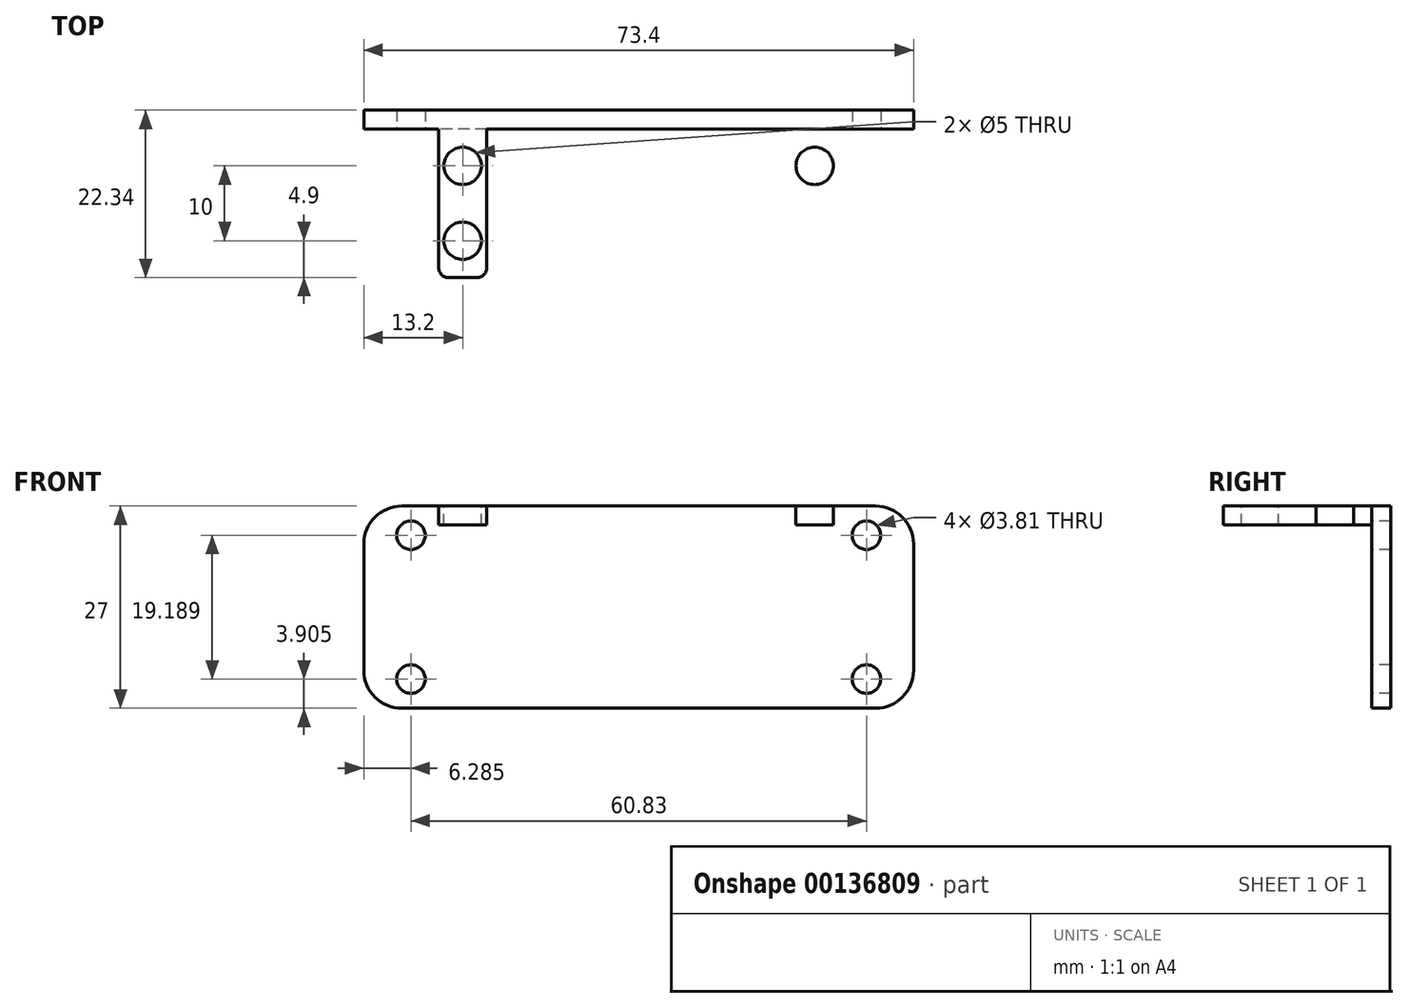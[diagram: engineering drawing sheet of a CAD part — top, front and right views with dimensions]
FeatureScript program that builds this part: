
annotation { "Feature Type Name" : "Feature", "Feature Type Description" : "" }
export const myFeature = defineFeature(function(context is Context, id is Id, definition is map)
    precondition{}
    {
        {
            var Q0;
            Q0=qCreatedBy(makeId("Top.planeOp"),FACE);
            var sketch = newSketch(context, id + "F0", { "sketchPlane" : qUnion([Q0])});
            skLineSegment(sketch, "E0.bottom", {"start": v(26.7, 1.27) * mm, "end": v(-26.7, 1.27) * mm});
            skLineSegment(sketch, "E0.top", {"start": v(26.7, -1.27) * mm, "end": v(-26.7, -1.27) * mm});
            skPoint(sketch, "E0.middle", {"position": v(0, 0) * mm});
            skLineSegment(sketch, "E1", {"start": v(-20.3, -1.27) * mm, "end": v(-20.3, -21.07) * mm});
            skLineSegment(sketch, "E2.bottom", {"start": v(-20.3, -21.07) * mm, "end": v(-26.7, -21.07) * mm});
            skLineSegment(sketch, "E2.top", {"start": v(-20.3, -1.27) * mm, "end": v(-26.7, -1.27) * mm});
            skLineSegment(sketch, "E2.left", {"start": v(-20.3, -21.07) * mm, "end": v(-20.3, -1.27) * mm});
            skLineSegment(sketch, "E2.right", {"start": v(-26.7, -21.07) * mm, "end": v(-26.7, -1.27) * mm});
            skCircle(sketch, "E3", {"center": v(-23.5, -6.17) * mm, "radius": 2.5 * mm});
            skCircle(sketch, "E4", {"center": v(-23.5, -16.17) * mm, "radius": 2.5 * mm});
            skLineSegment(sketch, "E5.bottom", {"start": v(-26.7, 1.27) * mm, "end": v(-36.7, 1.27) * mm});
            skLineSegment(sketch, "E5.top", {"start": v(-26.7, -1.27) * mm, "end": v(-36.7, -1.27) * mm});
            skLineSegment(sketch, "E5.right", {"start": v(-36.7, 1.27) * mm, "end": v(-36.7, -1.27) * mm});
            skLineSegment(sketch, "E6.MirrorCS", {"start": v(26.7, 1.27) * mm, "end": v(36.7, 1.27) * mm});
            skLineSegment(sketch, "E7.MirrorCS", {"start": v(36.7, 1.27) * mm, "end": v(36.7, -1.27) * mm});
            skLineSegment(sketch, "E8.MirrorCS", {"start": v(26.7, -1.27) * mm, "end": v(36.7, -1.27) * mm});
            skCircle(sketch, "E9.MirrorC", {"center": v(23.5, -6.17) * mm, "radius": 2.5 * mm});
            skLineSegment(sketch, "E10.MirrorCS", {"start": v(20.3, -21.07) * mm, "end": v(20.3, -1.27) * mm});
            skLineSegment(sketch, "E11.MirrorCS", {"start": v(26.7, -21.07) * mm, "end": v(26.7, -1.27) * mm});
            skLineSegment(sketch, "E12.MirrorCS", {"start": v(20.3, -21.07) * mm, "end": v(26.7, -21.07) * mm});
            skCircle(sketch, "E13.MirrorC", {"center": v(23.5, -16.17) * mm, "radius": 2.5 * mm});
            skSolve(sketch);
        }
        {
            var Q0;
            Q0=makeQuery(id+"F0.imprint","IMPRINT",FACE,{"disambiguationData":[TD([[makeQuery(id+"F0.imprint","IMPRINT",EDGE,{"derivedFrom":sQuery(id+"F0.wireOp",EDGE,"E0.bottom")}),1.0]])]});
            extrude(context, id + "F1", {"entities" : qUnion([Q0]), "oppositeDirection" : true, "depth" : 27 * mm});
        }
        {
            var Q0;
            Q0=makeQuery(id+"F0.imprint","IMPRINT",FACE,{"disambiguationData":[TD([[makeQuery(id+"F0.imprint","IMPRINT",EDGE,{"derivedFrom":sQuery(id+"F0.wireOp",EDGE,"E2.bottom")}),-1.0]])]});
            var Q1;
            Q1=makeQuery(id+"F0.imprint","IMPRINT",FACE,{"disambiguationData":[TD([[makeQuery(id+"F0.imprint","IMPRINT",EDGE,{"derivedFrom":sQuery(id+"F0.wireOp",EDGE,"E9.MirrorC")}),1.0]])]});
            extrude(context, id + "F2", {"entities" : qUnion([Q0, Q1]), "operationType" : NewBodyOperationType.ADD, "oppositeDirection" : true, "depth" : 2.54 * mm});
        }
        {
            var Q0;
            Q0=makeQuery(id+"F1.opExtrude","CAP_EDGE",EDGE,{"disambiguationData":[OSD([sQuery(id+"F0.wireOp",EDGE,"E5.right")])],"isStart":true});
            var Q1;
            Q1=makeQuery(id+"F1.opExtrude","CAP_EDGE",EDGE,{"disambiguationData":[OSD([sQuery(id+"F0.wireOp",EDGE,"E7.MirrorCS")])],"isStart":true});
            var Q2;
            Q2=makeQuery(id+"F1.opExtrude","CAP_EDGE",EDGE,{"disambiguationData":[OSD([sQuery(id+"F0.wireOp",EDGE,"E7.MirrorCS")])],"isStart":false});
            var Q3;
            Q3=makeQuery(id+"F1.opExtrude","CAP_EDGE",EDGE,{"disambiguationData":[OSD([sQuery(id+"F0.wireOp",EDGE,"E5.right")])],"isStart":false});
            fillet(context, id + "F3", {"entities" : qUnion([Q0, Q1, Q2, Q3]), "radius" : 5.08 * mm, "tangentPropagation" : true, "allowEdgeOverflow" : false});
        }
        {
            var Q0;
            Q0=makeQuery(id+"F1.opExtrude","SWEPT_FACE",FACE,{"disambiguationData":[OSD([sQuery(id+"F0.wireOp",EDGE,"E0.top"),sQuery(id+"F0.wireOp",EDGE,"E2.top"),sQuery(id+"F0.wireOp",EDGE,"E5.top"),sQuery(id+"F0.wireOp",EDGE,"E8.MirrorCS")])]});
            var sketch = newSketch(context, id + "F4", { "sketchPlane" : qUnion([Q0])});
            skLineSegment(sketch, "E14", {"start": v(0, 0) * mm, "end": v(0, -27) * mm});
            skLineSegment(sketch, "E15.bottom", {"start": v(30.42, -3.9) * mm, "end": v(-30.42, -3.9) * mm});
            skLineSegment(sketch, "E15.top", {"start": v(30.42, -23.1) * mm, "end": v(-30.42, -23.1) * mm});
            skLineSegment(sketch, "E15.left", {"start": v(30.42, -3.9) * mm, "end": v(30.42, -23.1) * mm});
            skLineSegment(sketch, "E15.right", {"start": v(-30.42, -3.9) * mm, "end": v(-30.42, -23.1) * mm});
            skPoint(sketch, "E15.middle", {"position": v(0, -13.5) * mm});
            skSolve(sketch);
        }
        {
            var Q0;
            Q0=sQuery(id+"F4.wireOp",VERTEX,"E15.right.start");
            var Q1;
            Q1=sQuery(id+"F4.wireOp",VERTEX,"E15.right.end");
            var Q2;
            Q2=sQuery(id+"F4.wireOp",VERTEX,"E15.left.start");
            var Q3;
            Q3=sQuery(id+"F4.wireOp",VERTEX,"E15.left.end");
            var Q4;
            Q4=makeQuery(id+"F1.opExtrude","SWEPT_BODY",BODY,{"disambiguationData":[OSD([sQuery(id+"F0.wireOp",EDGE,"E0.bottom"),sQuery(id+"F0.wireOp",EDGE,"E0.top"),sQuery(id+"F0.wireOp",EDGE,"E2.top"),sQuery(id+"F0.wireOp",EDGE,"E5.bottom"),sQuery(id+"F0.wireOp",EDGE,"E5.top"),sQuery(id+"F0.wireOp",EDGE,"E5.right"),sQuery(id+"F0.wireOp",EDGE,"E6.MirrorCS"),sQuery(id+"F0.wireOp",EDGE,"E7.MirrorCS"),sQuery(id+"F0.wireOp",EDGE,"E8.MirrorCS")])]});
            hole(context, id + "F5", {"style" : HoleStyle.SIMPLE, "endStyle" : HoleEndStyle.THROUGH, "holeDiameter" : 3.8 * mm, "locations" : qUnion([Q0, Q1, Q2, Q3]), "scope" : qUnion([Q4]), "isTappedThrough" : true});
        }
        {
            var Q0;
            Q0=makeQuery(id+"F2.opExtrude","SWEPT_EDGE",EDGE,{"disambiguationData":[OSD([sQuery(id+"F0.wireOp",EDGE,"E2.bottom"),sQuery(id+"F0.wireOp",EDGE,"E2.left")])]});
            var Q1;
            Q1=makeQuery(id+"F2.opExtrude","SWEPT_EDGE",EDGE,{"disambiguationData":[OSD([sQuery(id+"F0.wireOp",EDGE,"E2.bottom"),sQuery(id+"F0.wireOp",EDGE,"E2.right")])]});
            var Q2;
            Q2=makeQuery(id+"F2.opExtrude","SWEPT_EDGE",EDGE,{"disambiguationData":[OSD([sQuery(id+"F0.wireOp",EDGE,"E10.MirrorCS"),sQuery(id+"F0.wireOp",EDGE,"E12.MirrorCS")])]});
            var Q3;
            Q3=makeQuery(id+"F2.opExtrude","SWEPT_EDGE",EDGE,{"disambiguationData":[OSD([sQuery(id+"F0.wireOp",EDGE,"E11.MirrorCS"),sQuery(id+"F0.wireOp",EDGE,"E12.MirrorCS")])]});
            fillet(context, id + "F6", {"entities" : qUnion([Q0, Q1, Q2, Q3]), "radius" : 1.27 * mm, "tangentPropagation" : true, "allowEdgeOverflow" : false});
        }
    });
